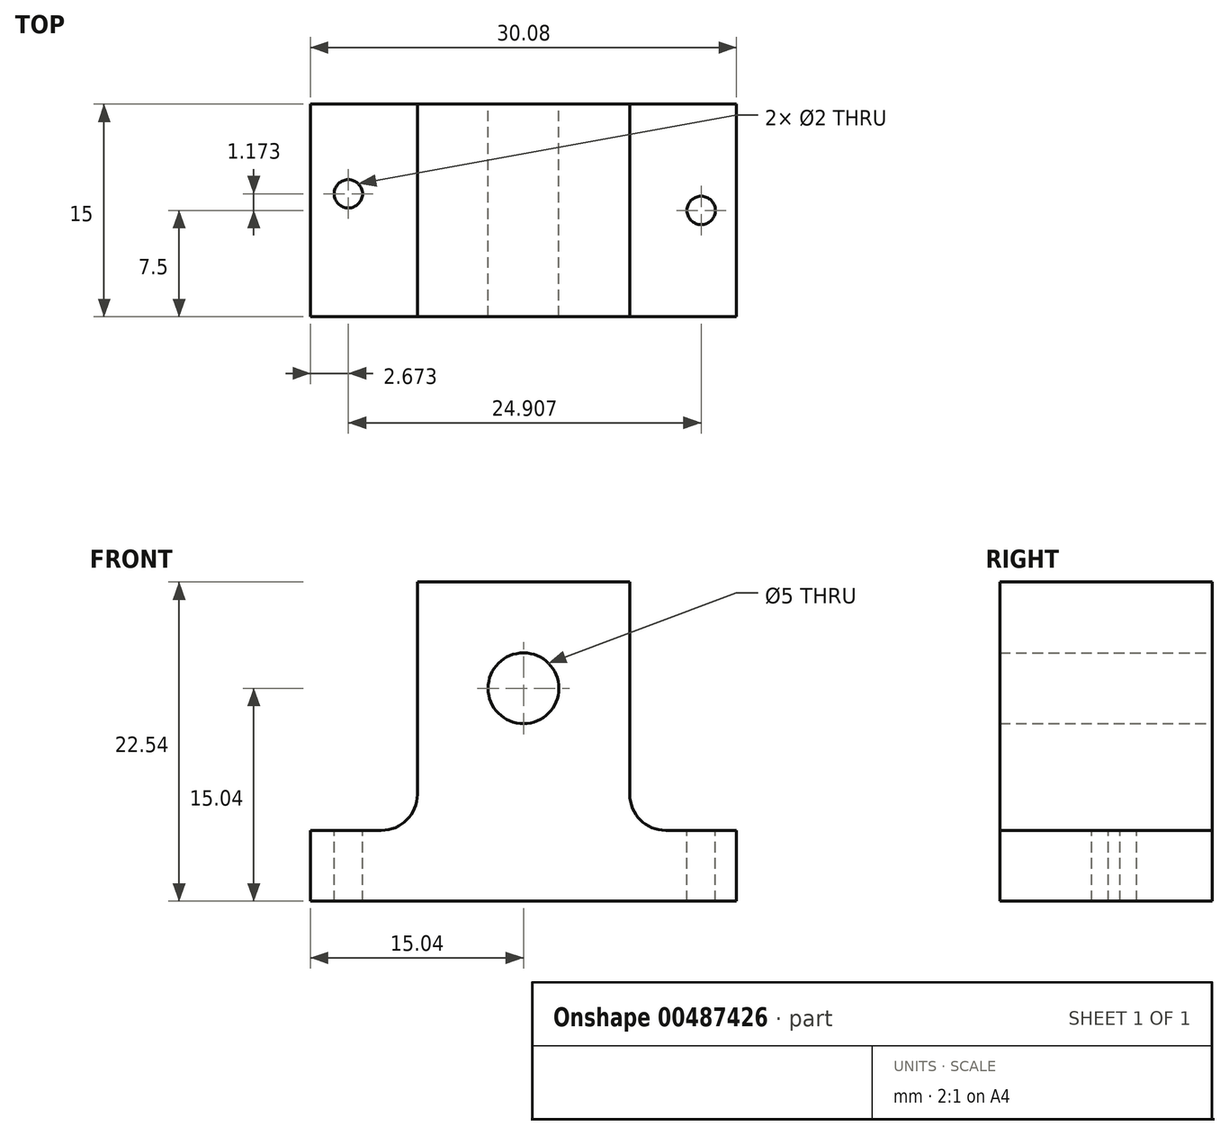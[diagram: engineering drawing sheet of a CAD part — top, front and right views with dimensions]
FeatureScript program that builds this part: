
annotation { "Feature Type Name" : "Feature", "Feature Type Description" : "" }
export const myFeature = defineFeature(function(context is Context, id is Id, definition is map)
    precondition{}
    {
        {
            var Q0;
            Q0=qCreatedBy(makeId("Front.planeOp"),FACE);
            var sketch = newSketch(context, id + "F0", { "sketchPlane" : qUnion([Q0])});
            skLineSegment(sketch, "E0", {"start": v(-44.68, 0) * mm, "end": v(-14.6, 0) * mm});
            skLineSegment(sketch, "E1", {"start": v(-14.6, 0) * mm, "end": v(-14.6, 5) * mm});
            skLineSegment(sketch, "E2", {"start": v(-14.6, 5) * mm, "end": v(-19.6, 5) * mm});
            skLineSegment(sketch, "E3", {"start": v(-22.14, 7.54) * mm, "end": v(-22.14, 22.54) * mm});
            skLineSegment(sketch, "E4", {"start": v(-22.14, 22.54) * mm, "end": v(-37.14, 22.54) * mm});
            skLineSegment(sketch, "E5", {"start": v(-37.14, 22.54) * mm, "end": v(-37.14, 7.54) * mm});
            skLineSegment(sketch, "E6", {"start": v(-39.68, 5) * mm, "end": v(-44.68, 5) * mm});
            skLineSegment(sketch, "E7", {"start": v(-44.68, 5) * mm, "end": v(-44.68, 0) * mm});
            skPoint(sketch, "E8.visualSharp", {"position": v(-22.14, 5) * mm});
            skArc(sketch, "E8.filletArc", {"start": v(-22.14, 7.54) * mm, "mid": v(-21.4, 5.74) * mm, "end": v(-19.6, 5) * mm});
            skPoint(sketch, "E9.visualSharp", {"position": v(-37.14, 5) * mm});
            skArc(sketch, "E9.filletArc", {"start": v(-39.68, 5) * mm, "mid": v(-37.88, 5.74) * mm, "end": v(-37.14, 7.54) * mm});
            skCircle(sketch, "E10", {"center": v(-29.64, 15.04) * mm, "radius": 2.5 * mm});
            skSolve(sketch);
        }
        {
            var Q0;
            Q0=makeQuery(id+"F0.imprint","IMPRINT",FACE,{"disambiguationData":[TD([[makeQuery(id+"F0.imprint","IMPRINT",EDGE,{"derivedFrom":sQuery(id+"F0.wireOp",EDGE,"E0")}),1.0]])]});
            extrude(context, id + "F1", {"entities" : qUnion([Q0]), "depth" : 15 * mm});
        }
        {
            var Q0;
            Q0=makeQuery(id+"F1.opExtrude","SWEPT_FACE",FACE,{"disambiguationData":[OSD([sQuery(id+"F0.wireOp",EDGE,"E2")])]});
            var sketch = newSketch(context, id + "F2", { "sketchPlane" : qUnion([Q0])});
            skCircle(sketch, "E11", {"center": v(-17.1, -7.5) * mm, "radius": 1 * mm});
            skCircle(sketch, "E12", {"center": v(-42, -6.33) * mm, "radius": 1 * mm});
            skSolve(sketch);
        }
        {
            var Q0;
            Q0=makeQuery(id+"F2.imprint","IMPRINT",FACE,{"disambiguationData":[TD([[makeQuery(id+"F2.imprint","IMPRINT",EDGE,{"derivedFrom":sQuery(id+"F2.wireOp",EDGE,"E11")}),1.0]])]});
            var Q1;
            Q1=makeQuery(id+"F2.imprint","IMPRINT",FACE,{"disambiguationData":[TD([[makeQuery(id+"F2.imprint","IMPRINT",EDGE,{"derivedFrom":sQuery(id+"F2.wireOp",EDGE,"E12")}),1.0]])]});
            extrude(context, id + "F3", {"entities" : qUnion([Q0, Q1]), "operationType" : NewBodyOperationType.REMOVE, "oppositeDirection" : true, "depth" : 5 * mm});
        }
    });
